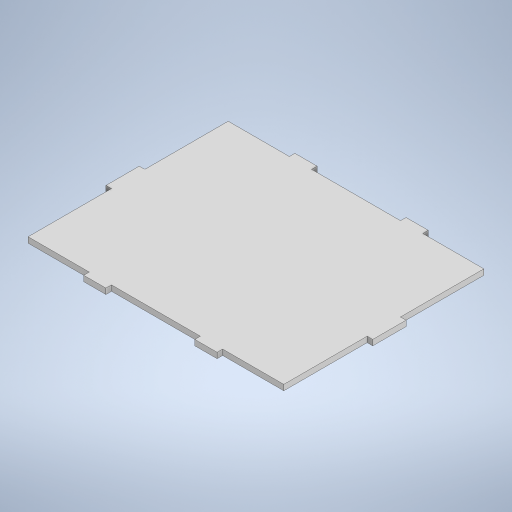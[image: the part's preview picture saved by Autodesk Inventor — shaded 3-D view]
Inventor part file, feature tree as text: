
AUTODESK INVENTOR PART (.ipt)
format: ipt  version: 2023 (Build 270158000, 158)  size: 251,392 bytes
history: native  units: mm
features: extrude x3, sketch x3
ambient origin geometry x8: Origin, YZ Plane, XZ Plane, XY Plane, X Axis, Y Axis, Z Axis, Center Point
bodies: Solid1 (feature_tree)
feature tree (6):
  extrude  "Extrusion1"  Depth=230.0mm
  extrude  "Extrusion2"  Depth=20.0mm
  extrude  "Extrusion3"  Depth=80.0mm
  sketch  "Sketch1"  dims[d0=180.0mm d1=230.0mm]
  sketch  "Sketch2"  dims[d2=5.0mm d3=0.0mm d4=20.0mm]
  sketch  "Sketch3"  dims[d5=20.0mm d6=80.0mm d7=55.0mm d8=55.0mm d9=5.0mm d10=185.0mm d11=0.0mm d12=0.0mm d13=30.0mm d14=75.0mm d15=5.0mm d16=235.0mm d17=0.0mm d18=0.0mm]
